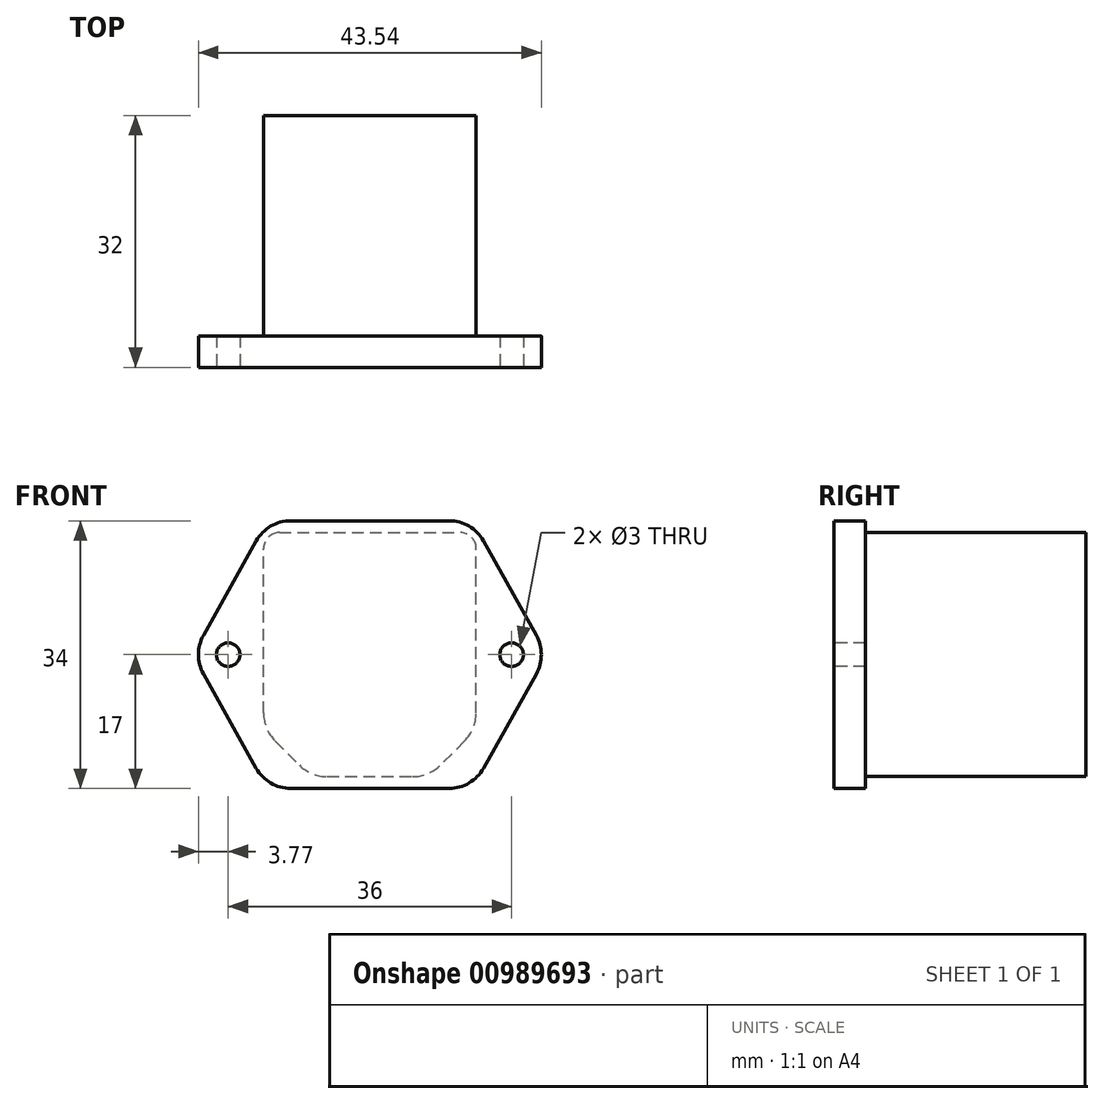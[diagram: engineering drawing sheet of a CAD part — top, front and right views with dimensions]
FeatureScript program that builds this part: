
annotation { "Feature Type Name" : "Feature", "Feature Type Description" : "" }
export const myFeature = defineFeature(function(context is Context, id is Id, definition is map)
    precondition{}
    {
        {
            var Q0;
            Q0=qCreatedBy(makeId("Front.planeOp"),FACE);
            var sketch = newSketch(context, id + "F0", { "sketchPlane" : qUnion([Q0])});
            skLineSegment(sketch, "E0.bottom", {"start": v(22.5, -17) * mm, "end": v(-22.5, -17) * mm});
            skLineSegment(sketch, "E0.top", {"start": v(22.5, 17) * mm, "end": v(-22.5, 17) * mm});
            skLineSegment(sketch, "E0.left", {"start": v(22.5, -17) * mm, "end": v(22.5, 17) * mm});
            skLineSegment(sketch, "E0.right", {"start": v(-22.5, -17) * mm, "end": v(-22.5, 17) * mm});
            skPoint(sketch, "E0.middle", {"position": v(0, 0) * mm});
            skLineSegment(sketch, "E1", {"start": v(-22.5, 0) * mm, "end": v(-13, 17) * mm});
            skLineSegment(sketch, "E2", {"start": v(-22.5, 0) * mm, "end": v(-13, -17) * mm});
            skLineSegment(sketch, "E3", {"start": v(22.5, 0) * mm, "end": v(13, 17) * mm});
            skLineSegment(sketch, "E4", {"start": v(22.5, 0) * mm, "end": v(13, -17) * mm});
            skSolve(sketch);
        }
        {
            var Q0;
            {var subQ0=sQuery(id+"F0.wireOp",EDGE,"E1");Q0=makeQuery(id+"F0.imprint","IMPRINT",FACE,{"disambiguationData":[TD([[makeQuery(id+"F0.imprint","IMPRINT",EDGE,{"derivedFrom":subQ0}),-1.0]])]});}
            extrude(context, id + "F1", {"entities" : qUnion([Q0]), "depth" : 4 * mm, "offsetDistance" : 25 * mm});
        }
        {
            var Q0;
            Q0=makeQuery(id+"F1.opExtrude","CAP_FACE",FACE,{"disambiguationData":[OSD([sQuery(id+"F0.wireOp",EDGE,"E0.bottom"),sQuery(id+"F0.wireOp",EDGE,"E0.top"),sQuery(id+"F0.wireOp",EDGE,"E1"),sQuery(id+"F0.wireOp",EDGE,"E2"),sQuery(id+"F0.wireOp",EDGE,"E3"),sQuery(id+"F0.wireOp",EDGE,"E4")])],"isStart":true});
            var sketch = newSketch(context, id + "F2", { "sketchPlane" : qUnion([Q0])});
            skLineSegment(sketch, "E5.bottom", {"start": v(13.5, -15.5) * mm, "end": v(-13.5, -15.5) * mm});
            skLineSegment(sketch, "E5.top", {"start": v(13.5, 15.5) * mm, "end": v(-13.5, 15.5) * mm});
            skLineSegment(sketch, "E5.left", {"start": v(13.5, -15.5) * mm, "end": v(13.5, 15.5) * mm});
            skLineSegment(sketch, "E5.right", {"start": v(-13.5, -15.5) * mm, "end": v(-13.5, 15.5) * mm});
            skPoint(sketch, "E5.middle", {"position": v(0, 0) * mm});
            skSolve(sketch);
        }
        {
            var Q0;
            {var subQ6=makeQuery(id+"F1.opExtrude","CAP_EDGE",EDGE,{"disambiguationData":[OSD([sQuery(id+"F0.wireOp",EDGE,"E2")])],"isStart":true});var subQ13=sQuery(id+"F2.wireOp",EDGE,"E5.bottom");var subQ14=makeQuery(id+"F2.imprint","INTERSECT",VERTEX,{"derivedFrom":[subQ6,subQ13]});Q0=makeQuery(id+"F2.imprint","IMPRINT",FACE,{"disambiguationData":[TD([[makeQuery(id+"F2.imprint","IMPRINT",EDGE,{"disambiguationData":[TD([[subQ14,-1.0]])],"derivedFrom":subQ13}),-1.0]])]});}
            extrude(context, id + "F3", {"entities" : qUnion([Q0]), "operationType" : NewBodyOperationType.ADD, "depth" : 28 * mm, "offsetDistance" : 25 * mm});
        }
        {
            var Q0;
            Q0=makeQuery(id+"F3.opExtrude","SWEPT_EDGE",EDGE,{"disambiguationData":[OSD([sQuery(id+"F2.wireOp",EDGE,"E5.top"),sQuery(id+"F2.wireOp",EDGE,"E5.left")])]});
            var Q1;
            Q1=makeQuery(id+"F3.opExtrude","SWEPT_EDGE",EDGE,{"disambiguationData":[OSD([sQuery(id+"F2.wireOp",EDGE,"E5.top"),sQuery(id+"F2.wireOp",EDGE,"E5.right")])]});
            fillet(context, id + "F4", {"entities" : qUnion([Q0, Q1]), "radius" : 2 * mm, "tangentPropagation" : true, "allowEdgeOverflow" : false});
        }
        {
            var Q0;
            Q0=makeQuery(id+"F1.opExtrude","SWEPT_EDGE",EDGE,{"disambiguationData":[OSD([sQuery(id+"F0.wireOp",EDGE,"E0.right"),sQuery(id+"F0.wireOp",EDGE,"E1"),sQuery(id+"F0.wireOp",EDGE,"E2")])]});
            var Q1;
            Q1=makeQuery(id+"F1.opExtrude","SWEPT_EDGE",EDGE,{"disambiguationData":[OSD([sQuery(id+"F0.wireOp",EDGE,"E0.left"),sQuery(id+"F0.wireOp",EDGE,"E3"),sQuery(id+"F0.wireOp",EDGE,"E4")])]});
            fillet(context, id + "F5", {"entities" : qUnion([Q0, Q1]), "radius" : 5 * mm, "tangentPropagation" : true, "allowEdgeOverflow" : false});
        }
        {
            var Q0;
            Q0=makeQuery(id+"F1.opExtrude","CAP_FACE",FACE,{"disambiguationData":[OSD([sQuery(id+"F0.wireOp",EDGE,"E0.bottom"),sQuery(id+"F0.wireOp",EDGE,"E0.top"),sQuery(id+"F0.wireOp",EDGE,"E1"),sQuery(id+"F0.wireOp",EDGE,"E2"),sQuery(id+"F0.wireOp",EDGE,"E3"),sQuery(id+"F0.wireOp",EDGE,"E4")])],"isStart":false});
            var sketch = newSketch(context, id + "F6", { "sketchPlane" : qUnion([Q0])});
            skCircle(sketch, "E6", {"center": v(-18, 0) * mm, "radius": 1.5 * mm});
            skPoint(sketch, "E6.centerSnap0", {"position": v(-21.77, 0) * mm});
            skCircle(sketch, "E7", {"center": v(18, 0) * mm, "radius": 1.5 * mm});
            skSolve(sketch);
        }
        {
            var Q0;
            Q0=makeQuery(id+"F6.imprint","IMPRINT",FACE,{"disambiguationData":[TD([[makeQuery(id+"F6.imprint","IMPRINT",EDGE,{"derivedFrom":sQuery(id+"F6.wireOp",EDGE,"E6")}),1.0]])]});
            var Q1;
            Q1=makeQuery(id+"F6.imprint","IMPRINT",FACE,{"disambiguationData":[TD([[makeQuery(id+"F6.imprint","IMPRINT",EDGE,{"derivedFrom":sQuery(id+"F6.wireOp",EDGE,"E7")}),1.0]])]});
            extrude(context, id + "F7", {"entities" : qUnion([Q0, Q1]), "operationType" : NewBodyOperationType.REMOVE, "oppositeDirection" : true, "depth" : 25 * mm, "offsetDistance" : 25 * mm});
        }
        {
            var Q0;
            Q0=makeQuery(id+"F3.opExtrude","SWEPT_EDGE",EDGE,{"disambiguationData":[OSD([sQuery(id+"F2.wireOp",EDGE,"E5.bottom"),sQuery(id+"F2.wireOp",EDGE,"E5.right")])]});
            var Q1;
            Q1=makeQuery(id+"F3.opExtrude","SWEPT_EDGE",EDGE,{"disambiguationData":[OSD([sQuery(id+"F2.wireOp",EDGE,"E5.bottom"),sQuery(id+"F2.wireOp",EDGE,"E5.left")])]});
            chamfer(context, id + "F8", {"entities" : qUnion([Q0, Q1]), "width" : 6 * mm, "tangentPropagation" : true});
        }
        {
            var Q0;
            Q0=makeQuery(id+"F1.opExtrude","SWEPT_EDGE",EDGE,{"disambiguationData":[OSD([sQuery(id+"F0.wireOp",EDGE,"E0.top"),sQuery(id+"F0.wireOp",EDGE,"E3")])]});
            var Q1;
            Q1=makeQuery(id+"F1.opExtrude","SWEPT_EDGE",EDGE,{"disambiguationData":[OSD([sQuery(id+"F0.wireOp",EDGE,"E0.top"),sQuery(id+"F0.wireOp",EDGE,"E1")])]});
            var Q2;
            Q2=makeQuery(id+"F1.opExtrude","SWEPT_EDGE",EDGE,{"disambiguationData":[OSD([sQuery(id+"F0.wireOp",EDGE,"E0.bottom"),sQuery(id+"F0.wireOp",EDGE,"E4")])]});
            var Q3;
            Q3=makeQuery(id+"F1.opExtrude","SWEPT_EDGE",EDGE,{"disambiguationData":[OSD([sQuery(id+"F0.wireOp",EDGE,"E0.bottom"),sQuery(id+"F0.wireOp",EDGE,"E2")])]});
            fillet(context, id + "F9", {"entities" : qUnion([Q0, Q1, Q2, Q3]), "radius" : 5 * mm, "tangentPropagation" : true, "allowEdgeOverflow" : false});
        }
        {
            var Q0;
            {var subQ0=sQuery(id+"F2.wireOp",EDGE,"E5.left");Q0=makeQuery(id+"F8.opChamfer","BLEND_EDGE",EDGE,{"blendedFrom":[makeQuery(id+"F3.opExtrude","SWEPT_EDGE",EDGE,{"disambiguationData":[OSD([sQuery(id+"F2.wireOp",EDGE,"E5.bottom"),subQ0])]}),makeQuery(id+"F3.opExtrude","SWEPT_FACE",FACE,{"disambiguationData":[OSD([subQ0])]})],"blendedInto":[makeQuery(id+"F3.opExtrude","SWEPT_FACE",FACE,{"disambiguationData":[OSD([subQ0])]})]});}
            var Q1;
            {var subQ0=sQuery(id+"F2.wireOp",EDGE,"E5.bottom");Q1=makeQuery(id+"F8.opChamfer","BLEND_EDGE",EDGE,{"blendedFrom":[makeQuery(id+"F3.opExtrude","SWEPT_EDGE",EDGE,{"disambiguationData":[OSD([subQ0,sQuery(id+"F2.wireOp",EDGE,"E5.left")])]}),makeQuery(id+"F3.opExtrude","SWEPT_FACE",FACE,{"disambiguationData":[OSD([subQ0])]})],"blendedInto":[makeQuery(id+"F3.opExtrude","SWEPT_FACE",FACE,{"disambiguationData":[OSD([subQ0])]})]});}
            var Q2;
            {var subQ0=sQuery(id+"F2.wireOp",EDGE,"E5.bottom");Q2=makeQuery(id+"F8.opChamfer","BLEND_EDGE",EDGE,{"blendedFrom":[makeQuery(id+"F3.opExtrude","SWEPT_EDGE",EDGE,{"disambiguationData":[OSD([subQ0,sQuery(id+"F2.wireOp",EDGE,"E5.right")])]}),makeQuery(id+"F3.opExtrude","SWEPT_FACE",FACE,{"disambiguationData":[OSD([subQ0])]})],"blendedInto":[makeQuery(id+"F3.opExtrude","SWEPT_FACE",FACE,{"disambiguationData":[OSD([subQ0])]})]});}
            var Q3;
            {var subQ0=sQuery(id+"F2.wireOp",EDGE,"E5.right");Q3=makeQuery(id+"F8.opChamfer","BLEND_EDGE",EDGE,{"blendedFrom":[makeQuery(id+"F3.opExtrude","SWEPT_EDGE",EDGE,{"disambiguationData":[OSD([sQuery(id+"F2.wireOp",EDGE,"E5.bottom"),subQ0])]}),makeQuery(id+"F3.opExtrude","SWEPT_FACE",FACE,{"disambiguationData":[OSD([subQ0])]})],"blendedInto":[makeQuery(id+"F3.opExtrude","SWEPT_FACE",FACE,{"disambiguationData":[OSD([subQ0])]})]});}
            fillet(context, id + "F10", {"entities" : qUnion([Q0, Q1, Q2, Q3]), "radius" : 5 * mm, "tangentPropagation" : true, "allowEdgeOverflow" : false});
        }
    });
